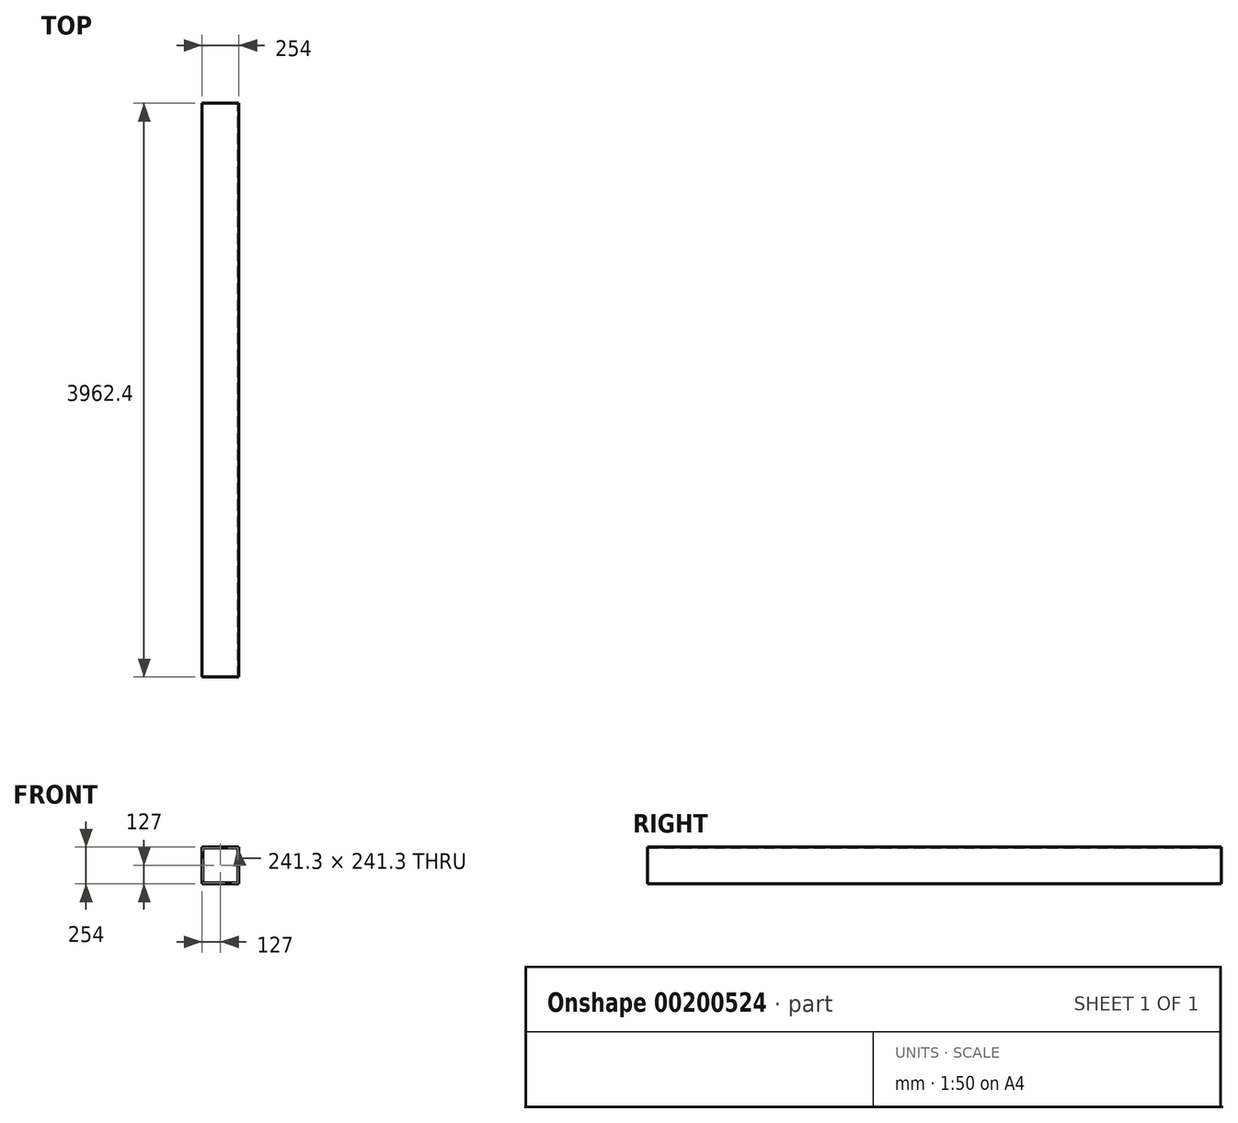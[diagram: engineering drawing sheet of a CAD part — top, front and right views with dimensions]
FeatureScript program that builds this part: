
annotation { "Feature Type Name" : "Feature", "Feature Type Description" : "" }
export const myFeature = defineFeature(function(context is Context, id is Id, definition is map)
    precondition{}
    {
        {
            assignVariable(context, id + "F0", {"name" : "ColumnHeight", "anyValue" : 3962.4 * mm});
        }
        {
            var Q0;
            Q0=qCreatedBy(makeId("Front.planeOp"),FACE);
            var sketch = newSketch(context, id + "F1", { "sketchPlane" : qUnion([Q0])});
            skLineSegment(sketch, "E0.bottom", {"start": v(-127, 0) * mm, "end": v(127, 0) * mm});
            skLineSegment(sketch, "E0.top", {"start": v(-127, 254) * mm, "end": v(127, 254) * mm});
            skLineSegment(sketch, "E0.left", {"start": v(-127, 0) * mm, "end": v(-127, 254) * mm});
            skLineSegment(sketch, "E0.right", {"start": v(127, 0) * mm, "end": v(127, 254) * mm});
            skLineSegment(sketch, "E1.bottom", {"start": v(-120.65, 247.65) * mm, "end": v(120.65, 247.65) * mm});
            skLineSegment(sketch, "E1.top", {"start": v(-120.65, 6.35) * mm, "end": v(120.65, 6.35) * mm});
            skLineSegment(sketch, "E1.left", {"start": v(-120.65, 247.65) * mm, "end": v(-120.65, 6.35) * mm});
            skLineSegment(sketch, "E1.right", {"start": v(120.65, 247.65) * mm, "end": v(120.65, 6.35) * mm});
            skSolve(sketch);
        }
        {
            var Q0;
            Q0=qSketchRegion(id+"F1",true);
            extrude(context, id + "F2", {"entities" : qUnion([Q0]), "depth" : getVariable(context, 'ColumnHeight'), "offsetDistance" : 25.4 * mm});
        }
    });
